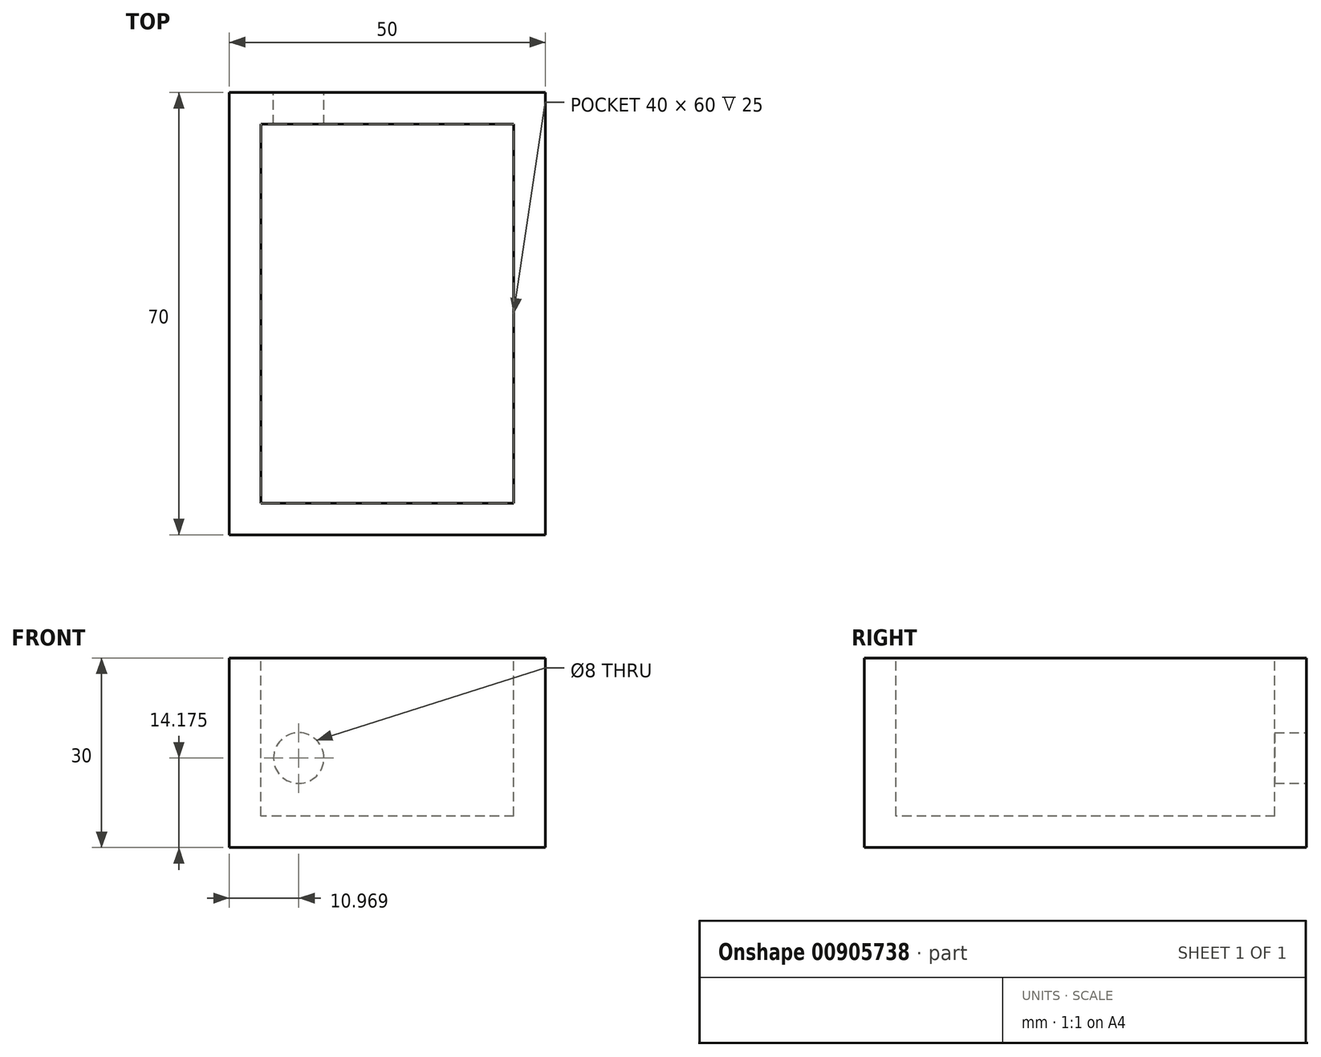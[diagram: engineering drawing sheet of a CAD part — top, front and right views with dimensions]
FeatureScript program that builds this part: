
annotation { "Feature Type Name" : "Feature", "Feature Type Description" : "" }
export const myFeature = defineFeature(function(context is Context, id is Id, definition is map)
    precondition{}
    {
        {
            var Q0;
            Q0=qCreatedBy(makeId("Top.planeOp"),FACE);
            var sketch = newSketch(context, id + "F0", { "sketchPlane" : qUnion([Q0])});
            skLineSegment(sketch, "E0.bottom", {"start": v(-25, 35) * mm, "end": v(25, 35) * mm});
            skLineSegment(sketch, "E0.top", {"start": v(-25, -35) * mm, "end": v(25, -35) * mm});
            skLineSegment(sketch, "E0.left", {"start": v(-25, 35) * mm, "end": v(-25, -35) * mm});
            skLineSegment(sketch, "E0.right", {"start": v(25, 35) * mm, "end": v(25, -35) * mm});
            skPoint(sketch, "E0.middle", {"position": v(0, 0) * mm});
            skLineSegment(sketch, "E1.bottom", {"start": v(20, 30) * mm, "end": v(-20, 30) * mm});
            skLineSegment(sketch, "E1.top", {"start": v(20, -30) * mm, "end": v(-20, -30) * mm});
            skLineSegment(sketch, "E1.left", {"start": v(20, 30) * mm, "end": v(20, -30) * mm});
            skLineSegment(sketch, "E1.right", {"start": v(-20, 30) * mm, "end": v(-20, -30) * mm});
            skSolve(sketch);
        }
        {
            var Q0;
            Q0=makeQuery(id+"F0.imprint","IMPRINT",FACE,{"disambiguationData":[TD([[makeQuery(id+"F0.imprint","IMPRINT",EDGE,{"derivedFrom":sQuery(id+"F0.wireOp",EDGE,"E0.bottom")}),-1.0]])]});
            var Q1;
            Q1=makeQuery(id+"F0.imprint","IMPRINT",FACE,{"disambiguationData":[TD([[makeQuery(id+"F0.imprint","IMPRINT",EDGE,{"derivedFrom":sQuery(id+"F0.wireOp",EDGE,"E1.bottom")}),1.0]])]});
            extrude(context, id + "F1", {"entities" : qUnion([Q0, Q1]), "depth" : 30 * mm, "offsetDistance" : 25 * mm});
        }
        {
            var Q0;
            Q0=makeQuery(id+"F1.opExtrude","CAP_FACE",FACE,{"disambiguationData":[OSD([sQuery(id+"F0.wireOp",EDGE,"E0.bottom"),sQuery(id+"F0.wireOp",EDGE,"E0.top"),sQuery(id+"F0.wireOp",EDGE,"E0.left"),sQuery(id+"F0.wireOp",EDGE,"E0.right")])],"isStart":false});
            var sketch = newSketch(context, id + "F2", { "sketchPlane" : qUnion([Q0])});
            skLineSegment(sketch, "E2.bottom", {"start": v(20, 30) * mm, "end": v(-20, 30) * mm});
            skLineSegment(sketch, "E2.top", {"start": v(20, -30) * mm, "end": v(-20, -30) * mm});
            skLineSegment(sketch, "E2.left", {"start": v(20, 30) * mm, "end": v(20, -30) * mm});
            skLineSegment(sketch, "E2.right", {"start": v(-20, 30) * mm, "end": v(-20, -30) * mm});
            skPoint(sketch, "E2.middle", {"position": v(0, 0) * mm});
            skSolve(sketch);
        }
        {
            var Q0;
            Q0=makeQuery(id+"F2.imprint","IMPRINT",FACE,{"disambiguationData":[TD([[makeQuery(id+"F2.imprint","IMPRINT",EDGE,{"derivedFrom":sQuery(id+"F2.wireOp",EDGE,"E2.bottom")}),1.0]])]});
            extrude(context, id + "F3", {"entities" : qUnion([Q0]), "operationType" : NewBodyOperationType.REMOVE, "oppositeDirection" : true, "depth" : 25 * mm, "offsetDistance" : 25 * mm});
        }
        {
            var Q0;
            Q0=makeQuery(id+"F1.opExtrude","SWEPT_FACE",FACE,{"disambiguationData":[OSD([sQuery(id+"F0.wireOp",EDGE,"E0.bottom")])]});
            var sketch = newSketch(context, id + "F4", { "sketchPlane" : qUnion([Q0])});
            skCircle(sketch, "E3", {"center": v(14.03, 14.18) * mm, "radius": 4 * mm});
            skSolve(sketch);
        }
        {
            var Q0;
            Q0 = qSketchRegion(id + "F4", true);
            var Q1;
            Q1=makeQuery(id+"F4.imprint","IMPRINT",FACE,{"disambiguationData":[TD([[makeQuery(id+"F4.imprint","IMPRINT",EDGE,{"derivedFrom":sQuery(id+"F4.wireOp",EDGE,"E3")}),1.0]])]});
            var Q2;
            Q2=makeQuery(id+"F3.boolean.opBoolean","COPY",FACE,{"derivedFrom":makeQuery(id+"F3.opExtrude","SWEPT_FACE",FACE,{"disambiguationData":[OSD([sQuery(id+"F2.wireOp",EDGE,"E2.bottom")])]})});
            extrude(context, id + "F5", {"entities" : qUnion([Q0, Q1]), "operationType" : NewBodyOperationType.REMOVE, "endBound" : BoundingType.UP_TO_SURFACE, "oppositeDirection" : true, "depth" : 25 * mm, "endBoundEntityFace" : qUnion([Q2]), "offsetDistance" : 25 * mm});
        }
    });
